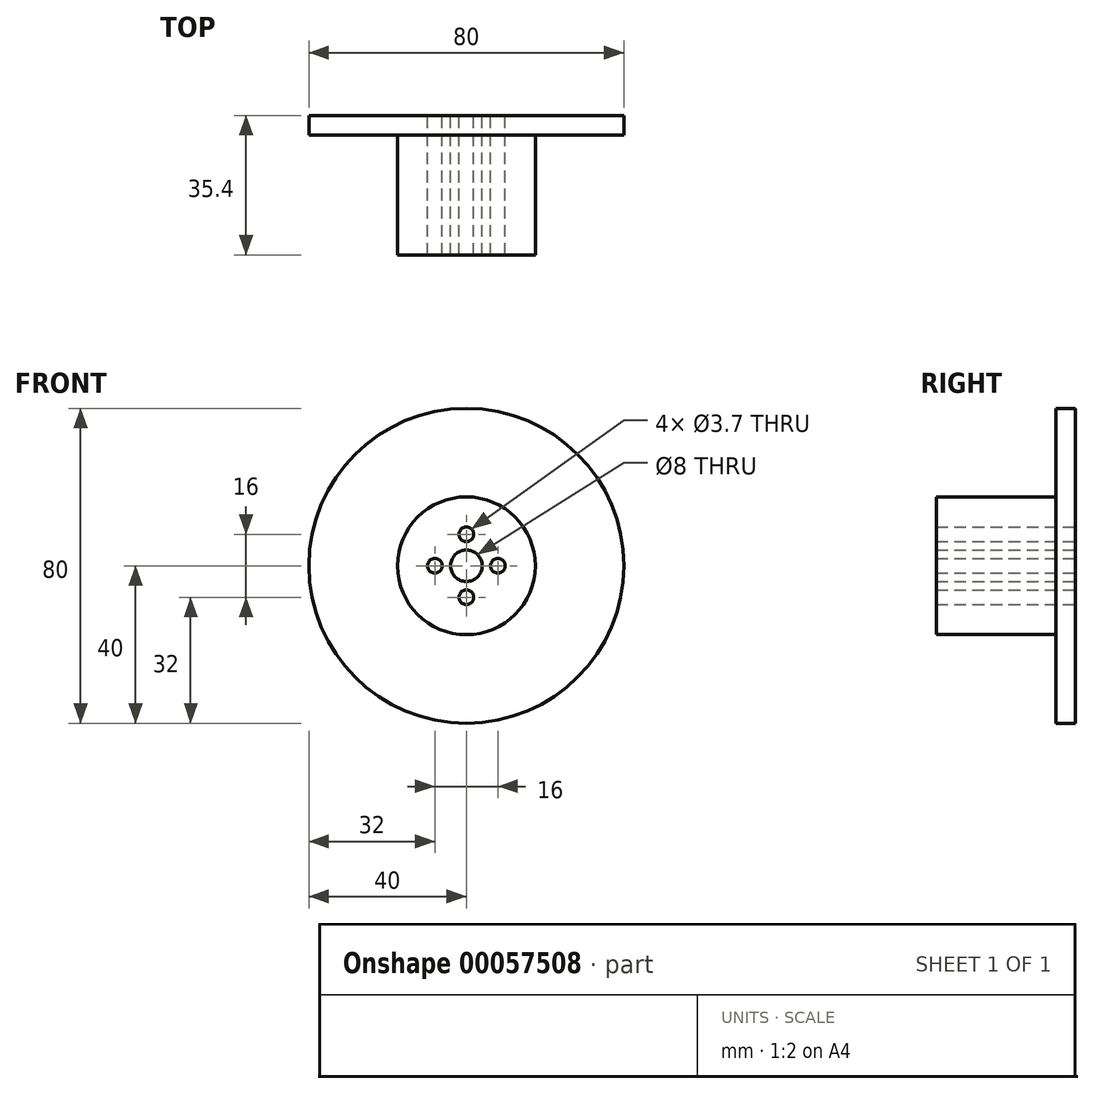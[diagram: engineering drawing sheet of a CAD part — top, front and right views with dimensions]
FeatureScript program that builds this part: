
annotation { "Feature Type Name" : "Feature", "Feature Type Description" : "" }
export const myFeature = defineFeature(function(context is Context, id is Id, definition is map)
    precondition{}
    {
        {
            var Q0;
            Q0=qCreatedBy(makeId("Right.planeOp"),FACE);
            var sketch = newSketch(context, id + "F0", { "sketchPlane" : qUnion([Q0])});
            skLineSegment(sketch, "E0.bottom", {"start": v(0, 0) * mm, "end": v(25.4, 0) * mm});
            skLineSegment(sketch, "E0.top", {"start": v(0, 17.5) * mm, "end": v(25.4, 17.5) * mm});
            skLineSegment(sketch, "E0.left", {"start": v(0, 0) * mm, "end": v(0, 17.5) * mm});
            skLineSegment(sketch, "E0.right", {"start": v(25.4, 0) * mm, "end": v(25.4, 17.5) * mm});
            skLineSegment(sketch, "E1.bottom", {"start": v(25.4, 0) * mm, "end": v(30.4, 0) * mm});
            skLineSegment(sketch, "E1.top", {"start": v(25.4, 40) * mm, "end": v(30.4, 40) * mm});
            skLineSegment(sketch, "E1.left", {"start": v(25.4, 0) * mm, "end": v(25.4, 40) * mm});
            skLineSegment(sketch, "E1.right", {"start": v(30.4, 0) * mm, "end": v(30.4, 40) * mm});
            skPoint(sketch, "E2.start.orphan", {"position": v(12.7, 0) * mm});
            skSolve(sketch);
        }
        {
            var Q0;
            {var subQ0=sQuery(id+"F0.wireOp",EDGE,"E0.bottom");Q0=makeQuery(id+"F0.imprint","IMPRINT",FACE,{"disambiguationData":[TD([[makeQuery(id+"F0.imprint","IMPRINT",EDGE,{"derivedFrom":subQ0}),1.0]])]});}
            var Q1;
            Q1=makeQuery(id+"F0.imprint","IMPRINT",FACE,{"disambiguationData":[TD([[makeQuery(id+"F0.imprint","IMPRINT",EDGE,{"derivedFrom":sQuery(id+"F0.wireOp",EDGE,"24fc3ebe-718f-49d8-8e15-73e93c458e6e0.MirrorCS")}),-1.0]])]});
            var Q2;
            {var subQ3=sQuery(id+"F0.wireOp",EDGE,"E1.bottom");Q2=makeQuery(id+"F0.imprint","IMPRINT",FACE,{"disambiguationData":[TD([[makeQuery(id+"F0.imprint","IMPRINT",EDGE,{"derivedFrom":subQ3}),1.0]])]});}
            var Q3;
            Q3=sQuery(id+"F0.wireOp",EDGE,"E0.bottom");
            revolve(context, id + "F1", {"entities" : qUnion([Q0, Q1, Q2]), "axis" : qUnion([Q3]), "revolveType" : RevolveType.FULL});
        }
        {
            var Q0;
            Q0=makeQuery(id+"F1.opRevolve","SWEPT_FACE",FACE,{"disambiguationData":[OSD([sQuery(id+"F0.wireOp",EDGE,"E1.right")])]});
            var sketch = newSketch(context, id + "F2", { "sketchPlane" : qUnion([Q0])});
            skCircle(sketch, "E3", {"center": v(0, 0) * mm, "radius": 4 * mm});
            skCircle(sketch, "E4", {"center": v(0, 8) * mm, "radius": 1.85 * mm});
            skCircle(sketch, "E5.1.0", {"center": v(-8, 0) * mm, "radius": 1.85 * mm});
            skCircle(sketch, "E5.2.0", {"center": v(0, -8) * mm, "radius": 1.85 * mm});
            skCircle(sketch, "E6.1.3.0", {"center": v(8, 0) * mm, "radius": 1.85 * mm});
            skSolve(sketch);
        }
        {
            var Q0;
            Q0=makeQuery(id+"F2.imprint","IMPRINT",FACE,{"disambiguationData":[TD([[makeQuery(id+"F2.imprint","IMPRINT",EDGE,{"derivedFrom":sQuery(id+"F2.wireOp",EDGE,"E4")}),1.0]])]});
            var Q1;
            Q1=makeQuery(id+"F2.imprint","IMPRINT",FACE,{"disambiguationData":[TD([[makeQuery(id+"F2.imprint","IMPRINT",EDGE,{"derivedFrom":sQuery(id+"F2.wireOp",EDGE,"E5.1.0")}),1.0]])]});
            var Q2;
            Q2=makeQuery(id+"F2.imprint","IMPRINT",FACE,{"disambiguationData":[TD([[makeQuery(id+"F2.imprint","IMPRINT",EDGE,{"derivedFrom":sQuery(id+"F2.wireOp",EDGE,"E3")}),1.0]])]});
            var Q3;
            Q3=makeQuery(id+"F2.imprint","IMPRINT",FACE,{"disambiguationData":[TD([[makeQuery(id+"F2.imprint","IMPRINT",EDGE,{"derivedFrom":sQuery(id+"F2.wireOp",EDGE,"E5.2.0")}),1.0]])]});
            var Q4;
            Q4=makeQuery(id+"F2.imprint","IMPRINT",FACE,{"disambiguationData":[TD([[makeQuery(id+"F2.imprint","IMPRINT",EDGE,{"derivedFrom":sQuery(id+"F2.wireOp",EDGE,"E6.1.3.0")}),1.0]])]});
            extrude(context, id + "F3", {"entities" : qUnion([Q0, Q1, Q2, Q3, Q4]), "operationType" : NewBodyOperationType.REMOVE, "oppositeDirection" : true, "depth" : 40 * mm});
        }
        {
            var Q0;
            Q0=makeQuery(id+"F1.opRevolve","SWEPT_FACE",FACE,{"disambiguationData":[OSD([sQuery(id+"F0.wireOp",EDGE,"E0.left")])]});
            extrude(context, id + "F4", {"entities" : qUnion([Q0]), "operationType" : NewBodyOperationType.ADD, "depth" : 5 * mm});
        }
    });
